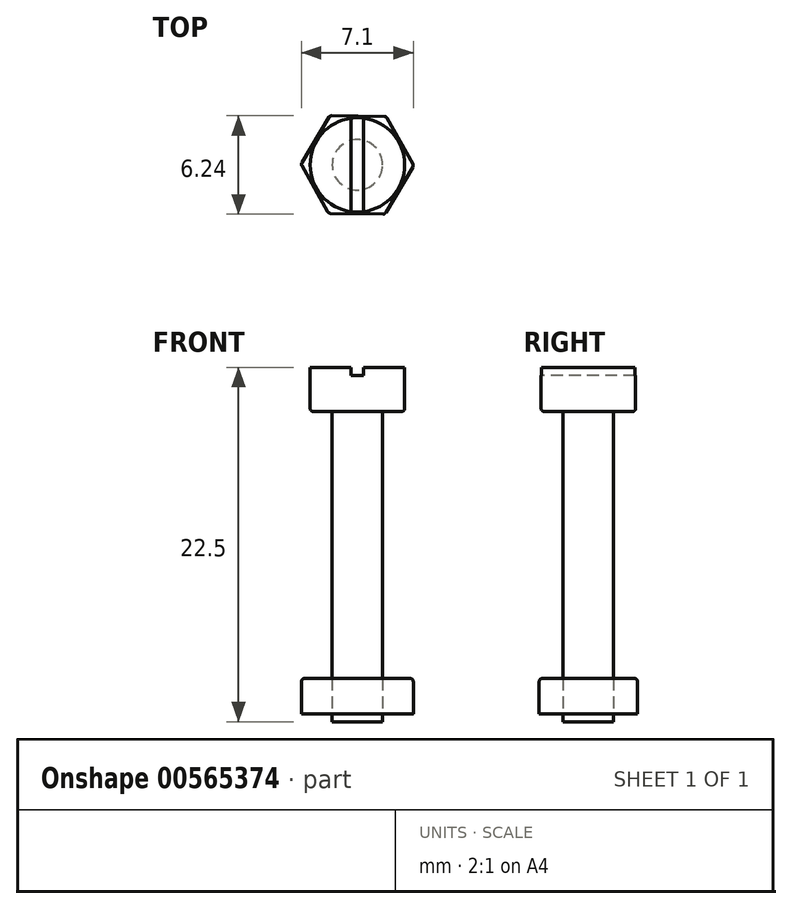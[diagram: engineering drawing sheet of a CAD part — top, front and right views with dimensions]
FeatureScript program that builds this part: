
annotation { "Feature Type Name" : "Feature", "Feature Type Description" : "" }
export const myFeature = defineFeature(function(context is Context, id is Id, definition is map)
    precondition{}
    {
        {
            var Q0;
            Q0=qCreatedBy(makeId("Top.planeOp"),FACE);
            var sketch = newSketch(context, id + "F0", { "sketchPlane" : qUnion([Q0])});
            skCircle(sketch, "E0.cCircle", {"center": v(0, 0) * mm, "radius": 3.1 * mm, "construction": true});
            skLineSegment(sketch, "E0.0", {"start": v(1.83, 3.08) * mm, "end": v(3.58, -0.05) * mm});
            skLineSegment(sketch, "E0.1", {"start": v(3.58, -0.05) * mm, "end": v(1.75, -3.12) * mm});
            skLineSegment(sketch, "E0.2", {"start": v(1.75, -3.12) * mm, "end": v(-1.83, -3.08) * mm});
            skLineSegment(sketch, "E0.3", {"start": v(-1.83, -3.08) * mm, "end": v(-3.58, 0.05) * mm});
            skLineSegment(sketch, "E0.4", {"start": v(-3.58, 0.05) * mm, "end": v(-1.75, 3.12) * mm});
            skLineSegment(sketch, "E0.5", {"start": v(-1.75, 3.12) * mm, "end": v(1.83, 3.08) * mm});
            skPoint(sketch, "E0.0.midPoint", {"position": v(2.7, 1.51) * mm});
            skSolve(sketch);
        }
        {
            var Q0;
            Q0=qSketchRegion(id+"F0",true);
            var Q1;
            Q1=qSketchRegion(id+"F4",true);
            extrude(context, id + "F1", {"entities" : qUnion([Q0, Q1]), "depth" : 2.25 * mm});
        }
        {
            var Q0;
            Q0=qCreatedBy(makeId("Top.planeOp"),FACE);
            var sketch = newSketch(context, id + "F2", { "sketchPlane" : qUnion([Q0])});
            skCircle(sketch, "E1", {"center": v(0, 0) * mm, "radius": 1.6 * mm});
            skSolve(sketch);
        }
        {
            var Q0;
            Q0=qSketchRegion(id+"F2",true);
            extrude(context, id + "F3", {"entities" : qUnion([Q0]), "depth" : 22 * mm, "hasSecondDirection" : true, "secondDirectionOppositeDirection" : true, "secondDirectionDepth" : 0.5 * mm});
        }
        {
            var Q0;
            Q0=makeQuery(id+"F3.opExtrude","CAP_FACE",FACE,{"disambiguationData":[OSD([sQuery(id+"F2.wireOp",EDGE,"E1")])],"isStart":false});
            var sketch = newSketch(context, id + "F4", { "sketchPlane" : qUnion([Q0])});
            skCircle(sketch, "E2", {"center": v(0, 0) * mm, "radius": 3 * mm});
            skLineSegment(sketch, "E3", {"start": v(-0.4, 2.97) * mm, "end": v(-0.4, -2.97) * mm});
            skLineSegment(sketch, "E4.MirrorCS", {"start": v(0.4, 2.97) * mm, "end": v(0.4, -2.97) * mm});
            skSolve(sketch);
        }
        {
            var Q0;
            Q0=qSketchRegion(id+"F4",true);
            extrude(context, id + "F5", {"entities" : qUnion([Q0]), "operationType" : NewBodyOperationType.ADD, "oppositeDirection" : true, "depth" : 2.8 * mm});
        }
        {
            var Q0;
            Q0=makeQuery(id+"F5.opExtrude","CAP_EDGE",EDGE,{"disambiguationData":[OSD([sQuery(id+"F4.wireOp",EDGE,"E2")])],"isStart":false});
            var Q1;
            Q1=makeQuery(id+"F1.opExtrude","CAP_EDGE",EDGE,{"disambiguationData":[OSD([sQuery(id+"F0.wireOp",EDGE,"E0.1")])],"isStart":false});
            var Q2;
            Q2=makeQuery(id+"F1.opExtrude","CAP_EDGE",EDGE,{"disambiguationData":[OSD([sQuery(id+"F0.wireOp",EDGE,"E0.0")])],"isStart":false});
            var Q3;
            Q3=makeQuery(id+"F1.opExtrude","CAP_EDGE",EDGE,{"disambiguationData":[OSD([sQuery(id+"F0.wireOp",EDGE,"E0.2")])],"isStart":false});
            var Q4;
            Q4=makeQuery(id+"F1.opExtrude","CAP_EDGE",EDGE,{"disambiguationData":[OSD([sQuery(id+"F0.wireOp",EDGE,"E0.3")])],"isStart":false});
            var Q5;
            Q5=makeQuery(id+"F1.opExtrude","CAP_EDGE",EDGE,{"disambiguationData":[OSD([sQuery(id+"F0.wireOp",EDGE,"E0.5")])],"isStart":false});
            var Q6;
            Q6=makeQuery(id+"F1.opExtrude","CAP_EDGE",EDGE,{"disambiguationData":[OSD([sQuery(id+"F0.wireOp",EDGE,"E0.4")])],"isStart":false});
            var Q7;
            Q7=makeQuery(id+"F1.opExtrude","SWEPT_EDGE",EDGE,{"disambiguationData":[OSD([sQuery(id+"F0.wireOp",EDGE,"E0.2"),sQuery(id+"F0.wireOp",EDGE,"E0.3")])]});
            var Q8;
            Q8=makeQuery(id+"F1.opExtrude","SWEPT_EDGE",EDGE,{"disambiguationData":[OSD([sQuery(id+"F0.wireOp",EDGE,"E0.1"),sQuery(id+"F0.wireOp",EDGE,"E0.2")])]});
            var Q9;
            Q9=makeQuery(id+"F1.opExtrude","SWEPT_EDGE",EDGE,{"disambiguationData":[OSD([sQuery(id+"F0.wireOp",EDGE,"E0.0"),sQuery(id+"F0.wireOp",EDGE,"E0.1")])]});
            var Q10;
            Q10=makeQuery(id+"F1.opExtrude","SWEPT_EDGE",EDGE,{"disambiguationData":[OSD([sQuery(id+"F0.wireOp",EDGE,"E0.3"),sQuery(id+"F0.wireOp",EDGE,"E0.4")])]});
            var Q11;
            Q11=makeQuery(id+"F1.opExtrude","SWEPT_EDGE",EDGE,{"disambiguationData":[OSD([sQuery(id+"F0.wireOp",EDGE,"E0.0"),sQuery(id+"F0.wireOp",EDGE,"E0.5")])]});
            var Q12;
            Q12=makeQuery(id+"F1.opExtrude","SWEPT_EDGE",EDGE,{"disambiguationData":[OSD([sQuery(id+"F0.wireOp",EDGE,"E0.4"),sQuery(id+"F0.wireOp",EDGE,"E0.5")])]});
            fillet(context, id + "F6", {"entities" : qUnion([Q0, Q1, Q2, Q3, Q4, Q5, Q6, Q7, Q8, Q9, Q10, Q11, Q12]), "radius" : 0.2 * mm, "tangentPropagation" : true, "allowEdgeOverflow" : false});
        }
        {
            var Q0;
            {var subQ0=sQuery(id+"F4.wireOp",EDGE,"E3");var subQ1=sQuery(id+"F4.wireOp",EDGE,"E2");var subQ2=makeQuery(id+"F4.imprint","INTERSECT",VERTEX,{"disambiguationData":[OD(0.0)],"derivedFrom":[subQ1,subQ0]});Q0=makeQuery(id+"F4.imprint","IMPRINT",FACE,{"disambiguationData":[TD([[makeQuery(id+"F4.imprint","IMPRINT",EDGE,{"disambiguationData":[TD([[subQ2,1.0]])],"derivedFrom":subQ1}),1.0]])]});}
            var Q1;
            {var subQ0=sQuery(id+"F4.wireOp",EDGE,"E3");var subQ1=makeQuery(id+"F3.opExtrude","CAP_EDGE",EDGE,{"disambiguationData":[OSD([sQuery(id+"F2.wireOp",EDGE,"E1")])],"isStart":false});var subQ2=makeQuery(id+"F4.imprint","INTERSECT",VERTEX,{"disambiguationData":[OD(0.0)],"derivedFrom":[subQ1,subQ0]});Q1=makeQuery(id+"F4.imprint","IMPRINT",FACE,{"disambiguationData":[TD([[makeQuery(id+"F4.imprint","IMPRINT",EDGE,{"disambiguationData":[TD([[subQ2,-1.0]])],"derivedFrom":subQ0}),1.0]])]});}
            var Q2;
            {var subQ0=sQuery(id+"F4.wireOp",EDGE,"E3");var subQ1=sQuery(id+"F4.wireOp",EDGE,"E2");var subQ2=makeQuery(id+"F4.imprint","INTERSECT",VERTEX,{"disambiguationData":[OD(1.0)],"derivedFrom":[subQ1,subQ0]});Q2=makeQuery(id+"F4.imprint","IMPRINT",FACE,{"disambiguationData":[TD([[makeQuery(id+"F4.imprint","IMPRINT",EDGE,{"disambiguationData":[TD([[subQ2,-1.0]])],"derivedFrom":subQ1}),1.0]])]});}
            extrude(context, id + "F7", {"entities" : qUnion([Q0, Q1, Q2]), "operationType" : NewBodyOperationType.REMOVE, "oppositeDirection" : true, "depth" : 0.5 * mm});
        }
    });
